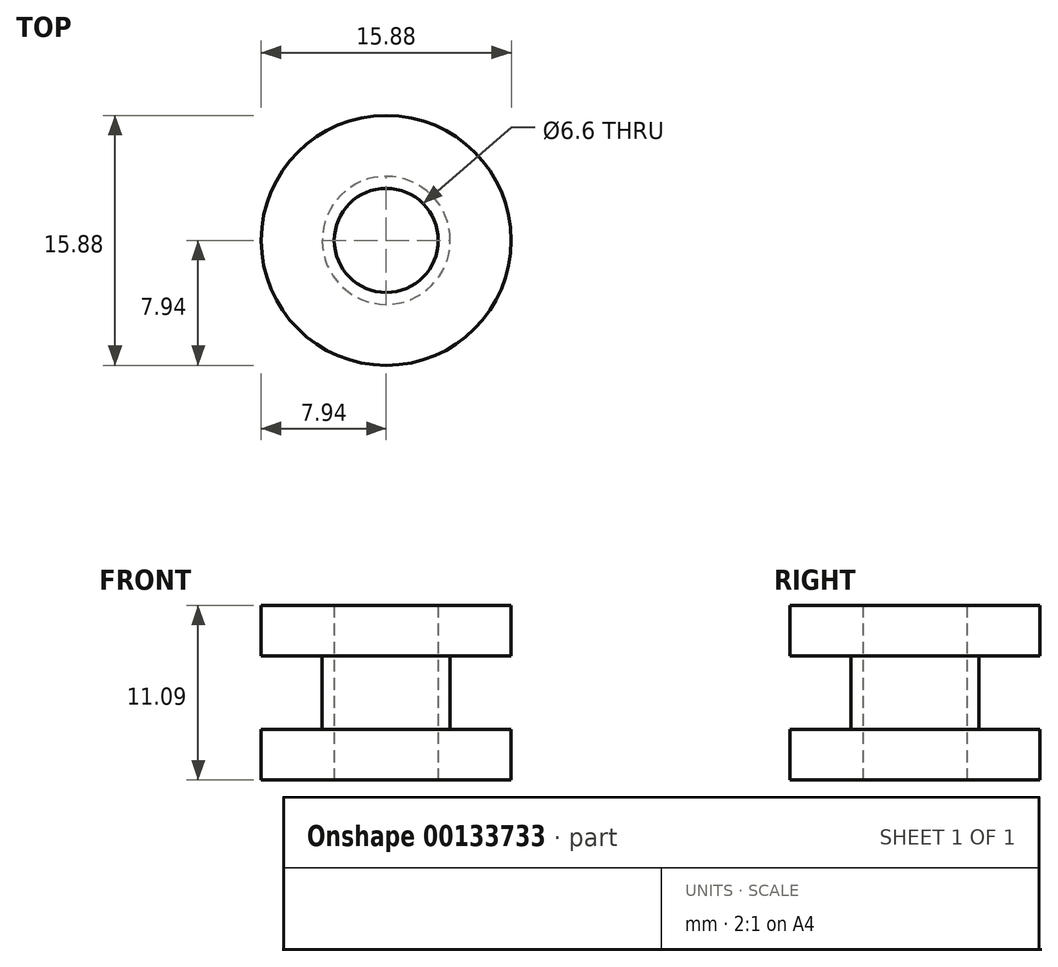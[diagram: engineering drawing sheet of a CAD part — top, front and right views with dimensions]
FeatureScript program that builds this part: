
annotation { "Feature Type Name" : "Feature", "Feature Type Description" : "" }
export const myFeature = defineFeature(function(context is Context, id is Id, definition is map)
    precondition{}
    {
        {
            var Q0;
            Q0=qCreatedBy(makeId("Top.planeOp"),FACE);
            var sketch = newSketch(context, id + "F0", { "sketchPlane" : qUnion([Q0])});
            skCircle(sketch, "E0", {"center": v(0, 0) * mm, "radius": 7.94 * mm});
            skCircle(sketch, "E1", {"center": v(0, 0) * mm, "radius": 4.06 * mm});
            skCircle(sketch, "E2", {"center": v(0, 0) * mm, "radius": 3.3 * mm});
            skSolve(sketch);
        }
        {
            var Q0;
            Q0=makeQuery(id+"F0.imprint","IMPRINT",FACE,{"disambiguationData":[TD([[makeQuery(id+"F0.imprint","IMPRINT",EDGE,{"derivedFrom":sQuery(id+"F0.wireOp",EDGE,"E1")}),1.0]])]});
            extrude(context, id + "F1", {"entities" : qUnion([Q0]), "depth" : 5.54 * mm});
        }
        {
            var Q0;
            Q0=makeQuery(id+"F0.imprint","IMPRINT",FACE,{"disambiguationData":[TD([[makeQuery(id+"F0.imprint","IMPRINT",EDGE,{"derivedFrom":sQuery(id+"F0.wireOp",EDGE,"E0")}),1.0]])]});
            extrude(context, id + "F2", {"entities" : qUnion([Q0]), "operationType" : NewBodyOperationType.ADD, "depth" : 3.2 * mm});
        }
        {
            var Q0;
            Q0=makeQuery(id+"F1.opExtrude","SWEPT_BODY",BODY,{"disambiguationData":[OSD([sQuery(id+"F0.wireOp",EDGE,"E1"),sQuery(id+"F0.wireOp",EDGE,"E2")])]});
            var Q1;
            Q1=makeQuery(id+"F1.opExtrude","CAP_FACE",FACE,{"disambiguationData":[OSD([sQuery(id+"F0.wireOp",EDGE,"E1"),sQuery(id+"F0.wireOp",EDGE,"E2")])],"isStart":false});
            mirror(context, id + "F3", {"operationType" : NewBodyOperationType.ADD, "entities" : qUnion([Q0]), "mirrorPlane" : qUnion([Q1])});
        }
    });
